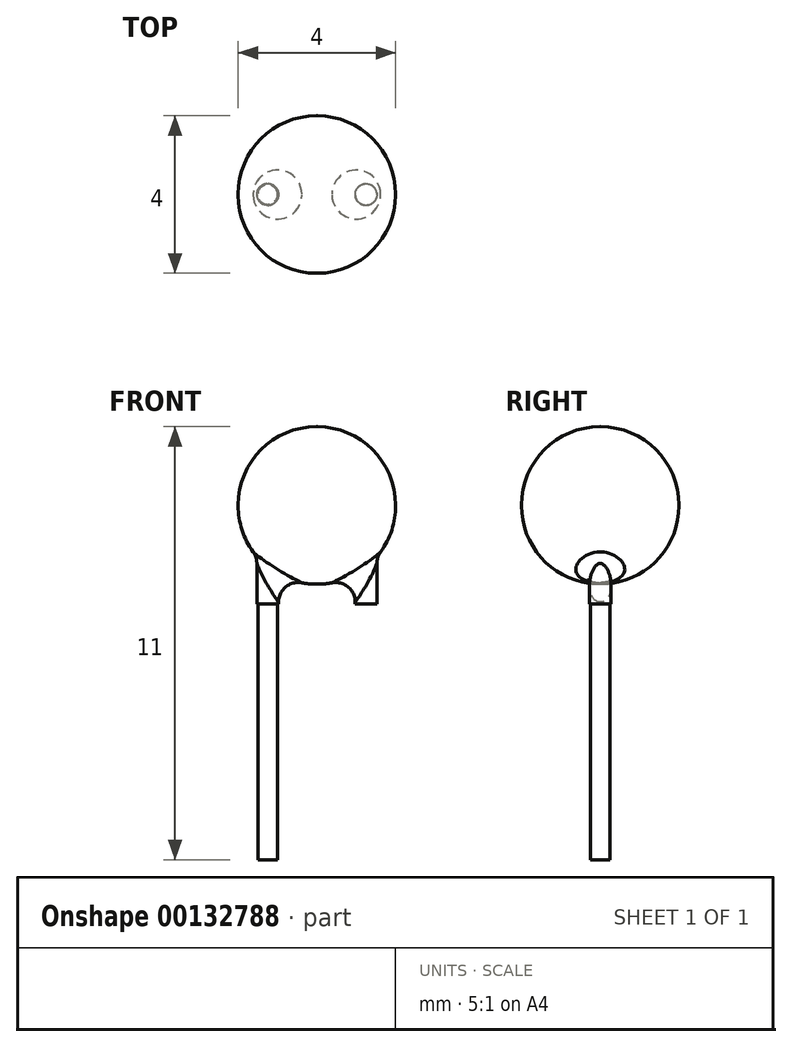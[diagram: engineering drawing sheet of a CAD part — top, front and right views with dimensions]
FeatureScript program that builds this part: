
annotation { "Feature Type Name" : "Feature", "Feature Type Description" : "" }
export const myFeature = defineFeature(function(context is Context, id is Id, definition is map)
    precondition{}
    {
        {
            var Q0;
            Q0=qCreatedBy(makeId("Front.planeOp"),FACE);
            var sketch = newSketch(context, id + "F0", { "sketchPlane" : qUnion([Q0])});
            skLineSegment(sketch, "E0.bottom", {"start": v(-2, 4) * mm, "end": v(2, 4) * mm});
            skLineSegment(sketch, "E0.top", {"start": v(-2, 8) * mm, "end": v(2, 8) * mm});
            skLineSegment(sketch, "E0.left", {"start": v(-2, 4) * mm, "end": v(-2, 8) * mm});
            skLineSegment(sketch, "E0.right", {"start": v(2, 4) * mm, "end": v(2, 8) * mm});
            skSolve(sketch);
        }
        {
            var Q0;
            Q0=makeQuery(id+"F0.imprint","IMPRINT",FACE,{"disambiguationData":[TD([[makeQuery(id+"F0.imprint","IMPRINT",EDGE,{"derivedFrom":sQuery(id+"F0.wireOp",EDGE,"E0.bottom")}),1.0]])]});
            extrude(context, id + "F1", {"entities" : qUnion([Q0]), "depth" : 2 * mm, "hasSecondDirection" : true, "secondDirectionOppositeDirection" : true, "secondDirectionDepth" : 2 * mm});
        }
        {
            var Q0;
            Q0=makeQuery(id+"F1.opExtrude","SWEPT_EDGE",EDGE,{"disambiguationData":[OSD([sQuery(id+"F0.wireOp",EDGE,"E0.top"),sQuery(id+"F0.wireOp",EDGE,"E0.right")])]});
            var Q1;
            Q1=makeQuery(id+"F1.opExtrude","SWEPT_EDGE",EDGE,{"disambiguationData":[OSD([sQuery(id+"F0.wireOp",EDGE,"E0.top"),sQuery(id+"F0.wireOp",EDGE,"E0.left")])]});
            var Q2;
            Q2=makeQuery(id+"F1.opExtrude","CAP_EDGE",EDGE,{"disambiguationData":[OSD([sQuery(id+"F0.wireOp",EDGE,"E0.bottom")])],"isStart":true});
            var Q3;
            Q3=makeQuery(id+"F1.opExtrude","CAP_EDGE",EDGE,{"disambiguationData":[OSD([sQuery(id+"F0.wireOp",EDGE,"E0.top")])],"isStart":true});
            var Q4;
            Q4=makeQuery(id+"F1.opExtrude","CAP_EDGE",EDGE,{"disambiguationData":[OSD([sQuery(id+"F0.wireOp",EDGE,"E0.top")])],"isStart":false});
            var Q5;
            Q5=makeQuery(id+"F1.opExtrude","CAP_EDGE",EDGE,{"disambiguationData":[OSD([sQuery(id+"F0.wireOp",EDGE,"E0.left")])],"isStart":true});
            var Q6;
            Q6=makeQuery(id+"F1.opExtrude","CAP_EDGE",EDGE,{"disambiguationData":[OSD([sQuery(id+"F0.wireOp",EDGE,"E0.right")])],"isStart":true});
            var Q7;
            Q7=makeQuery(id+"F1.opExtrude","SWEPT_EDGE",EDGE,{"disambiguationData":[OSD([sQuery(id+"F0.wireOp",EDGE,"E0.bottom"),sQuery(id+"F0.wireOp",EDGE,"E0.left")])]});
            var Q8;
            Q8=makeQuery(id+"F1.opExtrude","CAP_EDGE",EDGE,{"disambiguationData":[OSD([sQuery(id+"F0.wireOp",EDGE,"E0.left")])],"isStart":false});
            var Q9;
            Q9=makeQuery(id+"F1.opExtrude","SWEPT_EDGE",EDGE,{"disambiguationData":[OSD([sQuery(id+"F0.wireOp",EDGE,"E0.bottom"),sQuery(id+"F0.wireOp",EDGE,"E0.right")])]});
            var Q10;
            Q10=makeQuery(id+"F1.opExtrude","CAP_EDGE",EDGE,{"disambiguationData":[OSD([sQuery(id+"F0.wireOp",EDGE,"E0.bottom")])],"isStart":false});
            var Q11;
            Q11=makeQuery(id+"F1.opExtrude","CAP_EDGE",EDGE,{"disambiguationData":[OSD([sQuery(id+"F0.wireOp",EDGE,"E0.right")])],"isStart":false});
            fillet(context, id + "F2", {"entities" : qUnion([Q0, Q1, Q2, Q3, Q4, Q5, Q6, Q7, Q8, Q9, Q10, Q11]), "radius" : 1.99 * mm, "tangentPropagation" : true, "allowEdgeOverflow" : false});
        }
        {
            var Q0;
            Q0=qCreatedBy(makeId("Top.planeOp"),FACE);
            var sketch = newSketch(context, id + "F3", { "sketchPlane" : qUnion([Q0])});
            skCircle(sketch, "E1", {"center": v(-1.25, 0) * mm, "radius": 0.25 * mm});
            skCircle(sketch, "E2.MirrorC", {"center": v(1.25, 0) * mm, "radius": 0.25 * mm});
            skSolve(sketch);
        }
        {
            var Q0;
            Q0=makeQuery(id+"F3.imprint","IMPRINT",FACE,{"disambiguationData":[TD([[makeQuery(id+"F3.imprint","IMPRINT",EDGE,{"derivedFrom":sQuery(id+"F3.wireOp",EDGE,"E1")}),1.0]])]});
            var Q1;
            Q1=makeQuery(id+"F3.imprint","IMPRINT",FACE,{"disambiguationData":[TD([[makeQuery(id+"F3.imprint","IMPRINT",EDGE,{"derivedFrom":sQuery(id+"F3.wireOp",EDGE,"E2.MirrorC")}),-1.0]])]});
            extrude(context, id + "F4", {"entities" : qUnion([Q0, Q1]), "depth" : 3.5 * mm, "hasSecondDirection" : true, "secondDirectionOppositeDirection" : true, "secondDirectionDepth" : 3 * mm});
        }
        {
            var Q0;
            Q0=makeQuery(id+"F4.opExtrude","CAP_FACE",FACE,{"disambiguationData":[OSD([sQuery(id+"F3.wireOp",EDGE,"E1")])],"isStart":false});
            var sketch = newSketch(context, id + "F5", { "sketchPlane" : qUnion([Q0])});
            skCircle(sketch, "E3", {"center": v(1.25, 0) * mm, "radius": 0.28 * mm});
            skCircle(sketch, "E4.MirrorC", {"center": v(-1.25, 0) * mm, "radius": 0.28 * mm});
            skSolve(sketch);
        }
        {
            var Q0;
            Q0 = qSketchRegion(id + "F5", true);
            extrude(context, id + "F6", {"entities" : qUnion([Q0]), "operationType" : NewBodyOperationType.ADD, "depth" : 1.5 * mm});
        }
        {
            var Q0;
            {var subQ0=sQuery(id+"F0.wireOp",EDGE,"E0.left");var subQ1=sQuery(id+"F0.wireOp",EDGE,"E0.bottom");Q0=makeQuery(id+"F6.boolean.opBoolean","INTERSECT",EDGE,{"derivedFrom":[makeQuery(id+"F2.opFillet","BLEND_FACE",FACE,{"disambiguationData":[OSD([subQ1,subQ0]),TDD([makeQuery(id+"F1.opExtrude","CAP_VERTEX",VERTEX,{"disambiguationData":[OSD([subQ1,subQ0])],"isStart":false})])]}),makeQuery(id+"F6.opExtrude","SWEPT_FACE",FACE,{"disambiguationData":[OSD([sQuery(id+"F5.wireOp",EDGE,"E4.MirrorC")])]})]});}
            var Q1;
            {var subQ0=sQuery(id+"F0.wireOp",EDGE,"E0.right");var subQ1=sQuery(id+"F0.wireOp",EDGE,"E0.bottom");Q1=makeQuery(id+"F6.boolean.opBoolean","INTERSECT",EDGE,{"derivedFrom":[makeQuery(id+"F2.opFillet","BLEND_FACE",FACE,{"disambiguationData":[OSD([subQ1,subQ0]),TDD([makeQuery(id+"F1.opExtrude","CAP_VERTEX",VERTEX,{"disambiguationData":[OSD([subQ1,subQ0])],"isStart":false})])]}),makeQuery(id+"F6.opExtrude","SWEPT_FACE",FACE,{"disambiguationData":[OSD([sQuery(id+"F5.wireOp",EDGE,"E3")])]})]});}
            fillet(context, id + "F7", {"entities" : qUnion([Q0, Q1]), "radius" : 0.5 * mm, "tangentPropagation" : true, "allowEdgeOverflow" : false});
        }
    });
